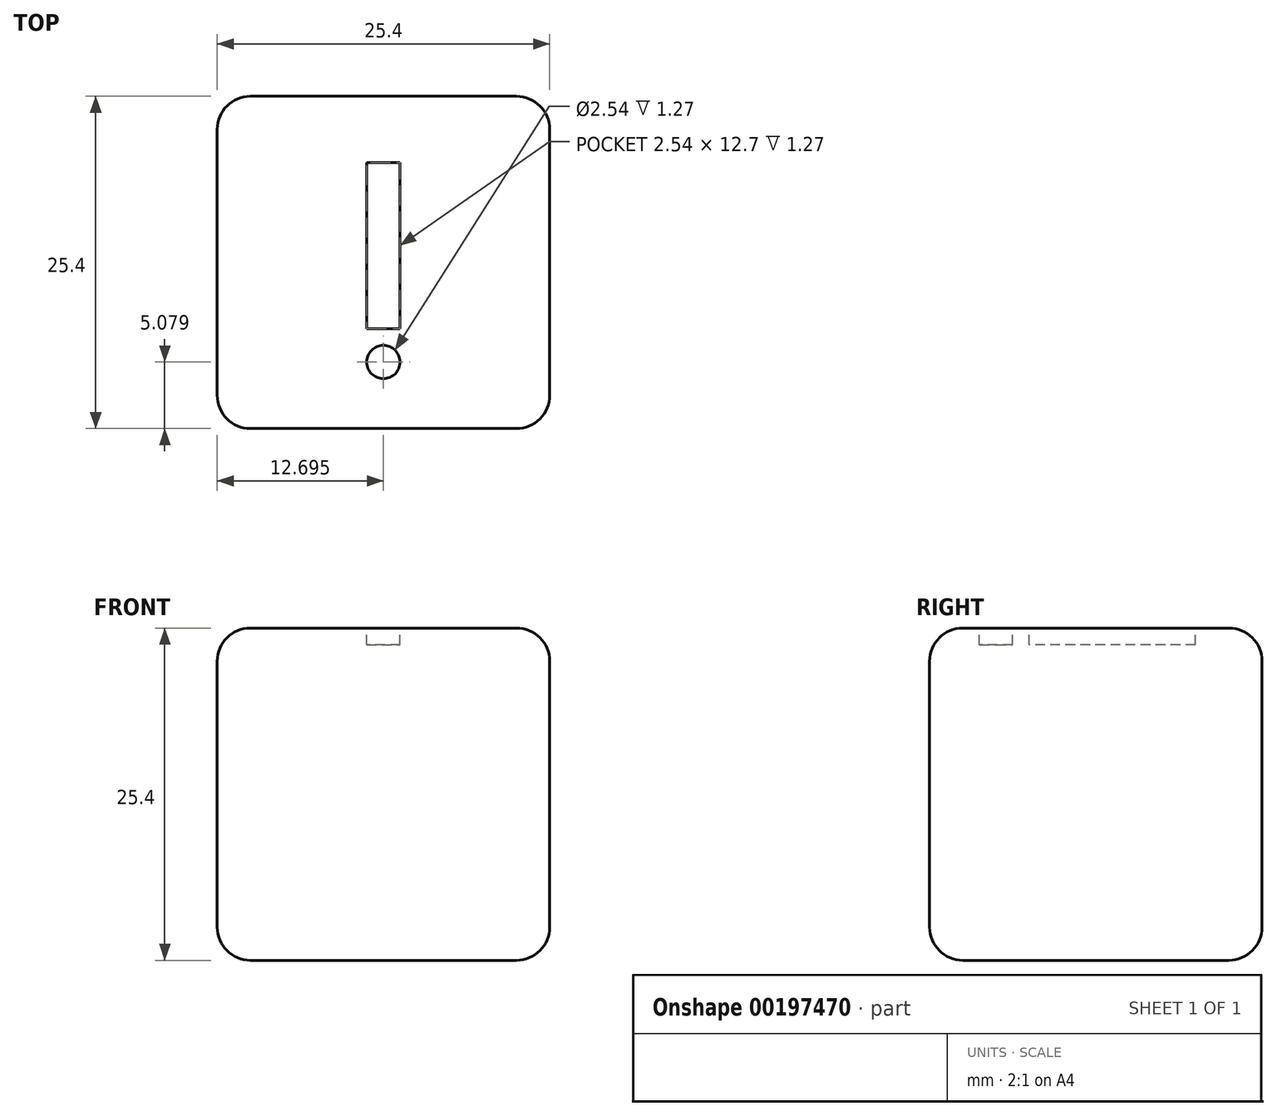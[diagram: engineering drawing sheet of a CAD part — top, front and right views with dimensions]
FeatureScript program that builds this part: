
annotation { "Feature Type Name" : "Feature", "Feature Type Description" : "" }
export const myFeature = defineFeature(function(context is Context, id is Id, definition is map)
    precondition{}
    {
        {
            var Q0;
            Q0=qCreatedBy(makeId("Top.planeOp"),FACE);
            var sketch = newSketch(context, id + "F0", { "sketchPlane" : qUnion([Q0])});
            skLineSegment(sketch, "E0.bottom", {"start": v(-9.93, 9.65) * mm, "end": v(15.47, 9.65) * mm});
            skLineSegment(sketch, "E0.top", {"start": v(-9.93, -15.75) * mm, "end": v(15.47, -15.75) * mm});
            skLineSegment(sketch, "E0.left", {"start": v(-9.93, 9.65) * mm, "end": v(-9.93, -15.75) * mm});
            skLineSegment(sketch, "E0.right", {"start": v(15.47, 9.65) * mm, "end": v(15.47, -15.75) * mm});
            skSolve(sketch);
        }
        {
            var Q0;
            Q0=makeQuery(id+"F0.imprint","IMPRINT",FACE,{"disambiguationData":[TD([[makeQuery(id+"F0.imprint","IMPRINT",EDGE,{"derivedFrom":sQuery(id+"F0.wireOp",EDGE,"E0.bottom")}),-1.0]])]});
            extrude(context, id + "F1", {"entities" : qUnion([Q0]), "depth" : 25.4 * mm});
        }
        {
            var Q0;
            Q0=makeQuery(id+"F1.opExtrude","CAP_EDGE",EDGE,{"disambiguationData":[OSD([sQuery(id+"F0.wireOp",EDGE,"E0.top")])],"isStart":false});
            var Q1;
            Q1=makeQuery(id+"F1.opExtrude","CAP_EDGE",EDGE,{"disambiguationData":[OSD([sQuery(id+"F0.wireOp",EDGE,"E0.right")])],"isStart":false});
            var Q2;
            Q2=makeQuery(id+"F1.opExtrude","SWEPT_EDGE",EDGE,{"disambiguationData":[OSD([sQuery(id+"F0.wireOp",EDGE,"E0.top"),sQuery(id+"F0.wireOp",EDGE,"E0.right")])]});
            var Q3;
            Q3=makeQuery(id+"F1.opExtrude","CAP_EDGE",EDGE,{"disambiguationData":[OSD([sQuery(id+"F0.wireOp",EDGE,"E0.right")])],"isStart":true});
            var Q4;
            Q4=makeQuery(id+"F1.opExtrude","CAP_EDGE",EDGE,{"disambiguationData":[OSD([sQuery(id+"F0.wireOp",EDGE,"E0.top")])],"isStart":true});
            var Q5;
            Q5=makeQuery(id+"F1.opExtrude","SWEPT_EDGE",EDGE,{"disambiguationData":[OSD([sQuery(id+"F0.wireOp",EDGE,"E0.top"),sQuery(id+"F0.wireOp",EDGE,"E0.left")])]});
            var Q6;
            Q6=makeQuery(id+"F1.opExtrude","CAP_EDGE",EDGE,{"disambiguationData":[OSD([sQuery(id+"F0.wireOp",EDGE,"E0.left")])],"isStart":true});
            var Q7;
            Q7=makeQuery(id+"F1.opExtrude","CAP_EDGE",EDGE,{"disambiguationData":[OSD([sQuery(id+"F0.wireOp",EDGE,"E0.bottom")])],"isStart":true});
            var Q8;
            Q8=makeQuery(id+"F1.opExtrude","CAP_EDGE",EDGE,{"disambiguationData":[OSD([sQuery(id+"F0.wireOp",EDGE,"E0.bottom")])],"isStart":false});
            var Q9;
            Q9=makeQuery(id+"F1.opExtrude","CAP_EDGE",EDGE,{"disambiguationData":[OSD([sQuery(id+"F0.wireOp",EDGE,"E0.left")])],"isStart":false});
            var Q10;
            Q10=makeQuery(id+"F1.opExtrude","SWEPT_EDGE",EDGE,{"disambiguationData":[OSD([sQuery(id+"F0.wireOp",EDGE,"E0.bottom"),sQuery(id+"F0.wireOp",EDGE,"E0.left")])]});
            var Q11;
            Q11=makeQuery(id+"F1.opExtrude","SWEPT_EDGE",EDGE,{"disambiguationData":[OSD([sQuery(id+"F0.wireOp",EDGE,"E0.bottom"),sQuery(id+"F0.wireOp",EDGE,"E0.right")])]});
            fillet(context, id + "F2", {"entities" : qUnion([Q0, Q1, Q2, Q3, Q4, Q5, Q6, Q7, Q8, Q9, Q10, Q11]), "radius" : 2.54 * mm, "tangentPropagation" : true, "allowEdgeOverflow" : false});
        }
        {
            var Q0;
            Q0=makeQuery(id+"F1.opExtrude","CAP_FACE",FACE,{"disambiguationData":[OSD([sQuery(id+"F0.wireOp",EDGE,"E0.bottom"),sQuery(id+"F0.wireOp",EDGE,"E0.top"),sQuery(id+"F0.wireOp",EDGE,"E0.left"),sQuery(id+"F0.wireOp",EDGE,"E0.right")])],"isStart":false});
            var sketch = newSketch(context, id + "F3", { "sketchPlane" : qUnion([Q0])});
            skCircle(sketch, "E1", {"center": v(2.77, -10.67) * mm, "radius": 1.27 * mm});
            skLineSegment(sketch, "E2.bottom", {"start": v(1.5, 4.57) * mm, "end": v(4.04, 4.57) * mm});
            skLineSegment(sketch, "E2.top", {"start": v(1.5, -8.13) * mm, "end": v(4.04, -8.13) * mm});
            skLineSegment(sketch, "E2.left", {"start": v(1.5, 4.57) * mm, "end": v(1.5, -8.13) * mm});
            skLineSegment(sketch, "E2.right", {"start": v(4.04, 4.57) * mm, "end": v(4.04, -8.13) * mm});
            skSolve(sketch);
        }
        {
            var Q0;
            Q0=makeQuery(id+"F3.imprint","IMPRINT",FACE,{"disambiguationData":[TD([[makeQuery(id+"F3.imprint","IMPRINT",EDGE,{"derivedFrom":sQuery(id+"F3.wireOp",EDGE,"E2.bottom")}),-1.0]])]});
            var Q1;
            Q1=makeQuery(id+"F3.imprint","IMPRINT",FACE,{"disambiguationData":[TD([[makeQuery(id+"F3.imprint","IMPRINT",EDGE,{"derivedFrom":sQuery(id+"F3.wireOp",EDGE,"E1")}),1.0]])]});
            extrude(context, id + "F4", {"entities" : qUnion([Q0, Q1]), "operationType" : NewBodyOperationType.REMOVE, "oppositeDirection" : true, "depth" : 1.27 * mm});
        }
    });
